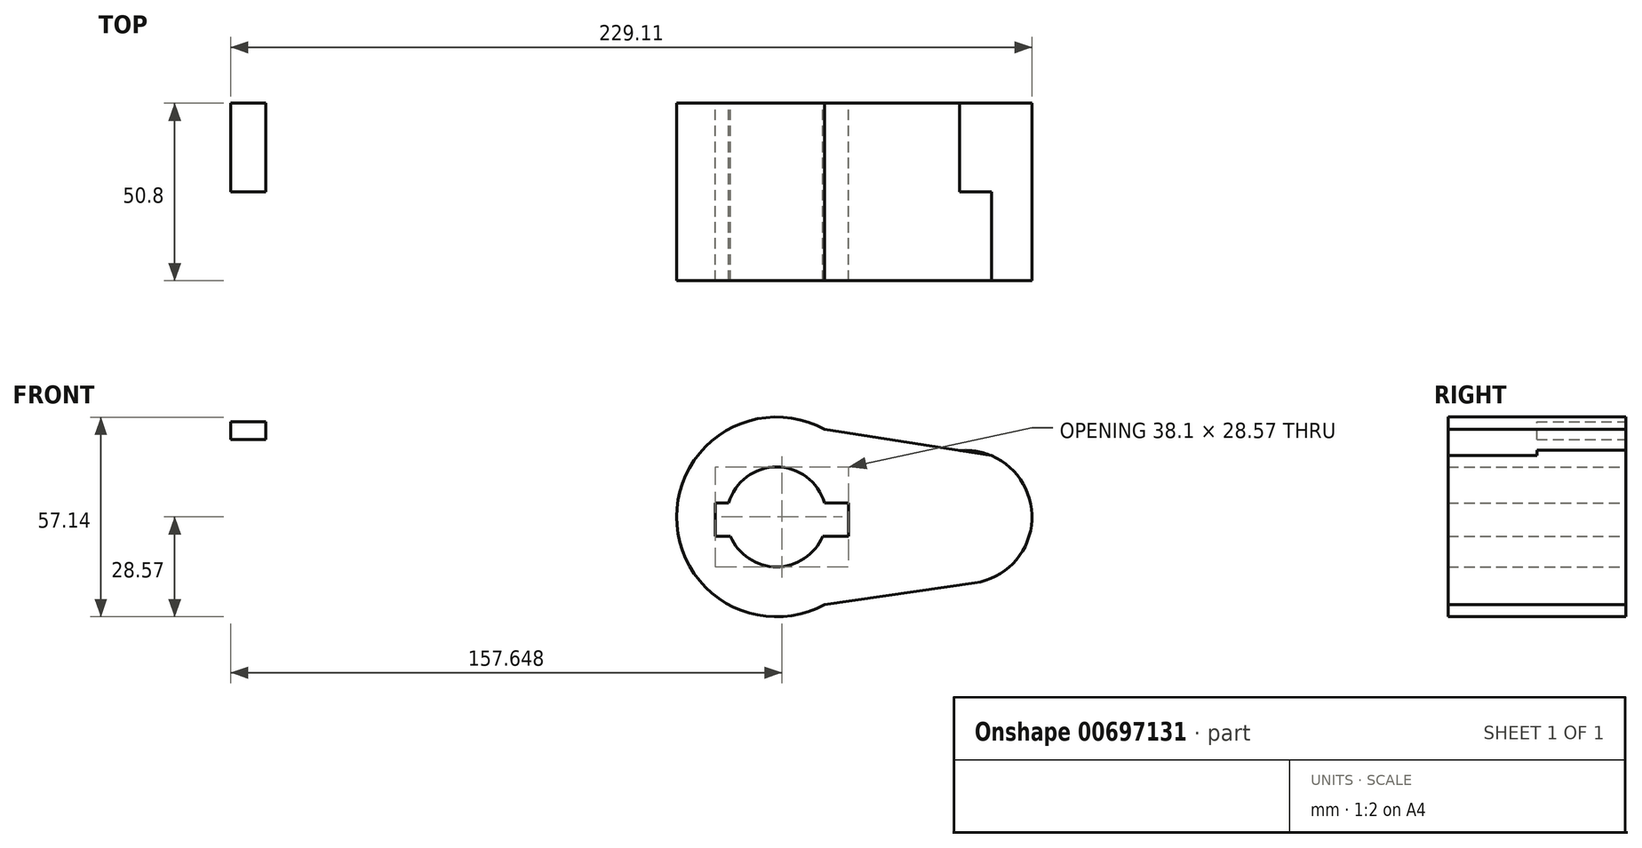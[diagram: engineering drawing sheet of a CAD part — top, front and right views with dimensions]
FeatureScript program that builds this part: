
annotation { "Feature Type Name" : "Feature", "Feature Type Description" : "" }
export const myFeature = defineFeature(function(context is Context, id is Id, definition is map)
    precondition{}
    {
        {
            var Q0;
            Q0=qCreatedBy(makeId("Front.planeOp"),FACE);
            var sketch = newSketch(context, id + "F0", { "sketchPlane" : qUnion([Q0])});
            skCircle(sketch, "E0", {"center": v(0, 0) * mm, "radius": 28.58 * mm});
            skCircle(sketch, "E1", {"center": v(53.98, 0) * mm, "radius": 19.05 * mm});
            skLineSegment(sketch, "E2", {"start": v(13.71, 25.07) * mm, "end": v(61.44, 17.53) * mm});
            skLineSegment(sketch, "E3", {"start": v(13.71, -25.07) * mm, "end": v(61.47, -18.16) * mm});
            skCircle(sketch, "E4", {"center": v(0, 0) * mm, "radius": 14.29 * mm});
            skCircle(sketch, "E5", {"center": v(53.98, 0) * mm, "radius": 14.29 * mm});
            skLineSegment(sketch, "E6.bottom", {"start": v(-17.48, 4.01) * mm, "end": v(20.62, 4.01) * mm});
            skLineSegment(sketch, "E6.top", {"start": v(-17.48, -5.51) * mm, "end": v(20.62, -5.51) * mm});
            skLineSegment(sketch, "E6.left", {"start": v(-17.48, 4.01) * mm, "end": v(-17.48, -5.51) * mm});
            skLineSegment(sketch, "E6.right", {"start": v(20.62, 4.01) * mm, "end": v(20.62, -5.51) * mm});
            skLineSegment(sketch, "E7.bottom", {"start": v(-146, 22.2) * mm, "end": v(-156.08, 22.2) * mm});
            skLineSegment(sketch, "E7.top", {"start": v(-146, 27.25) * mm, "end": v(-156.08, 27.25) * mm});
            skLineSegment(sketch, "E7.left", {"start": v(-146, 22.2) * mm, "end": v(-146, 27.25) * mm});
            skLineSegment(sketch, "E7.right", {"start": v(-156.08, 22.2) * mm, "end": v(-156.08, 27.25) * mm});
            skSolve(sketch);
        }
        {
            var Q0;
            {var subQ4=sQuery(id+"F0.wireOp",EDGE,"E6.left");Q0=makeQuery(id+"F0.imprint","IMPRINT",FACE,{"disambiguationData":[TD([[makeQuery(id+"F0.imprint","IMPRINT",EDGE,{"derivedFrom":subQ4}),-1.0]])]});}
            var Q1;
            {var subQ0=sQuery(id+"F0.wireOp",EDGE,"E2");var subQ1=sQuery(id+"F0.wireOp",EDGE,"E0");var subQ2=makeQuery(id+"F0.imprint","INTERSECT",VERTEX,{"derivedFrom":[subQ1,subQ0]});Q1=makeQuery(id+"F0.imprint","IMPRINT",FACE,{"disambiguationData":[TD([[makeQuery(id+"F0.imprint","IMPRINT",EDGE,{"disambiguationData":[TD([[subQ2,1.0]])],"derivedFrom":subQ1}),-1.0]])]});}
            var Q2;
            Q2=makeQuery(id+"F0.imprint","IMPRINT",FACE,{"disambiguationData":[TD([[makeQuery(id+"F0.imprint","IMPRINT",EDGE,{"derivedFrom":sQuery(id+"F0.wireOp",EDGE,"E5")}),1.0]])]});
            var Q3;
            Q3=makeQuery(id+"F0.imprint","IMPRINT",FACE,{"disambiguationData":[TD([[makeQuery(id+"F0.imprint","IMPRINT",EDGE,{"derivedFrom":sQuery(id+"F0.wireOp",EDGE,"E5")}),-1.0]])]});
            extrude(context, id + "F1", {"entities" : qUnion([Q0, Q1, Q2, Q3]), "depth" : 25.4 * mm, "offsetDistance" : 25.4 * mm});
        }
        {
            var Q0;
            {var subQ4=sQuery(id+"F0.wireOp",EDGE,"E6.left");Q0=makeQuery(id+"F0.imprint","IMPRINT",FACE,{"disambiguationData":[TD([[makeQuery(id+"F0.imprint","IMPRINT",EDGE,{"derivedFrom":subQ4}),-1.0]])]});}
            extrude(context, id + "F2", {"entities" : qUnion([Q0]), "operationType" : NewBodyOperationType.ADD, "depth" : 25.4 * mm, "offsetDistance" : 25.4 * mm});
        }
        {
            var Q0;
            {var subQ0=sQuery(id+"F0.wireOp",EDGE,"E2");var subQ1=sQuery(id+"F0.wireOp",EDGE,"E0");var subQ2=makeQuery(id+"F0.imprint","INTERSECT",VERTEX,{"derivedFrom":[subQ1,subQ0]});Q0=makeQuery(id+"F0.imprint","IMPRINT",FACE,{"disambiguationData":[TD([[makeQuery(id+"F0.imprint","IMPRINT",EDGE,{"disambiguationData":[TD([[subQ2,1.0]])],"derivedFrom":subQ1}),-1.0]])]});}
            var Q1;
            {var subQ4=sQuery(id+"F0.wireOp",EDGE,"E6.left");Q1=makeQuery(id+"F0.imprint","IMPRINT",FACE,{"disambiguationData":[TD([[makeQuery(id+"F0.imprint","IMPRINT",EDGE,{"derivedFrom":subQ4}),-1.0]])]});}
            var Q2;
            Q2=makeQuery(id+"F0.imprint","IMPRINT",FACE,{"disambiguationData":[TD([[makeQuery(id+"F0.imprint","IMPRINT",EDGE,{"derivedFrom":sQuery(id+"F0.wireOp",EDGE,"E5")}),-1.0]])]});
            extrude(context, id + "F3", {"entities" : qUnion([Q0, Q1, Q2]), "operationType" : NewBodyOperationType.ADD, "depth" : 25.4 * mm, "offsetDistance" : 25.4 * mm});
        }
        {
            var Q0;
            Q0=makeQuery(id+"F1.opExtrude","CAP_FACE",FACE,{"disambiguationData":[OSD([sQuery(id+"F0.wireOp",EDGE,"E0"),sQuery(id+"F0.wireOp",EDGE,"E1"),sQuery(id+"F0.wireOp",EDGE,"E2"),sQuery(id+"F0.wireOp",EDGE,"E3"),sQuery(id+"F0.wireOp",EDGE,"E4"),sQuery(id+"F0.wireOp",EDGE,"E6.bottom"),sQuery(id+"F0.wireOp",EDGE,"E6.top"),sQuery(id+"F0.wireOp",EDGE,"E6.left"),sQuery(id+"F0.wireOp",EDGE,"E6.right")])],"isStart":false});
            var sketch = newSketch(context, id + "F4", { "sketchPlane" : qUnion([Q0])});
            skSolve(sketch);
        }
        {
            var Q0;
            Q0=makeQuery(id+"F4.imprint","IMPRINT",FACE,{"disambiguationData":[TD([[makeQuery(id+"F4.imprint","IMPRINT",EDGE,{"derivedFrom":makeQuery(id+"F1.opExtrude","CAP_EDGE",EDGE,{"disambiguationData":[OSD([sQuery(id+"F0.wireOp",EDGE,"E0")])],"isStart":false})}),1.0]])]});
            var Q1;
            Q1 = qSketchRegion(id + "F0", true);
            extrude(context, id + "F5", {"entities" : qUnion([Q0, Q1]), "operationType" : NewBodyOperationType.ADD, "depth" : 25.4 * mm, "offsetDistance" : 25.4 * mm});
        }
    });
